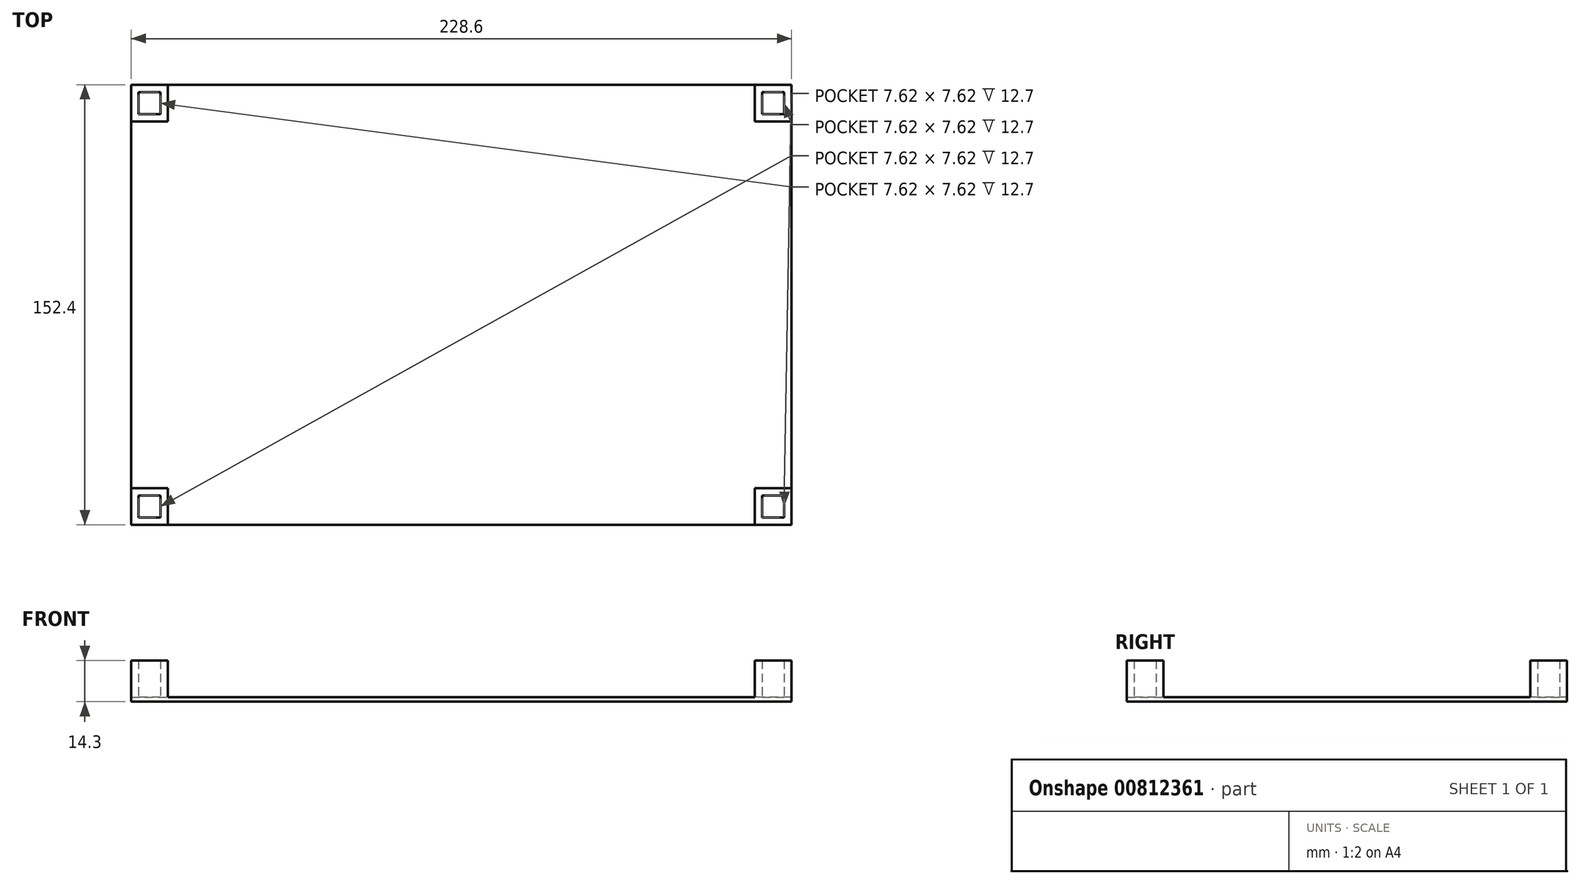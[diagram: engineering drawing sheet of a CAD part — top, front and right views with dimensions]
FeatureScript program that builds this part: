
annotation { "Feature Type Name" : "Feature", "Feature Type Description" : "" }
export const myFeature = defineFeature(function(context is Context, id is Id, definition is map)
    precondition{}
    {
        {
            var Q0;
            Q0=qCreatedBy(makeId("Top.planeOp"),FACE);
            var sketch = newSketch(context, id + "F0", { "sketchPlane" : qUnion([Q0])});
            skLineSegment(sketch, "E0.bottom", {"start": v(114.3, -76.2) * mm, "end": v(-114.3, -76.2) * mm});
            skLineSegment(sketch, "E0.top", {"start": v(114.3, 76.2) * mm, "end": v(-114.3, 76.2) * mm});
            skLineSegment(sketch, "E0.left", {"start": v(114.3, -76.2) * mm, "end": v(114.3, 76.2) * mm});
            skLineSegment(sketch, "E0.right", {"start": v(-114.3, -76.2) * mm, "end": v(-114.3, 76.2) * mm});
            skPoint(sketch, "E0.middle", {"position": v(0, 0) * mm});
            skSolve(sketch);
        }
        {
            var Q0;
            Q0=makeQuery(id+"F0.imprint","IMPRINT",FACE,{"disambiguationData":[TD([[makeQuery(id+"F0.imprint","IMPRINT",EDGE,{"derivedFrom":sQuery(id+"F0.wireOp",EDGE,"E0.bottom")}),-1.0]])]});
            extrude(context, id + "F1", {"entities" : qUnion([Q0]), "depth" : 1.6 * mm, "offsetDistance" : 25.4 * mm});
        }
        {
            var Q0;
            Q0=makeQuery(id+"F1.opExtrude","CAP_FACE",FACE,{"disambiguationData":[OSD([sQuery(id+"F0.wireOp",EDGE,"E0.bottom"),sQuery(id+"F0.wireOp",EDGE,"E0.top"),sQuery(id+"F0.wireOp",EDGE,"E0.left"),sQuery(id+"F0.wireOp",EDGE,"E0.right")])],"isStart":false});
            var sketch = newSketch(context, id + "F2", { "sketchPlane" : qUnion([Q0])});
            skLineSegment(sketch, "E1.bottom", {"start": v(114.3, -76.2) * mm, "end": v(101.6, -76.2) * mm});
            skLineSegment(sketch, "E1.top", {"start": v(114.3, -63.5) * mm, "end": v(101.6, -63.5) * mm});
            skLineSegment(sketch, "E1.left", {"start": v(114.3, -76.2) * mm, "end": v(114.3, -63.5) * mm});
            skLineSegment(sketch, "E1.right", {"start": v(101.6, -76.2) * mm, "end": v(101.6, -63.5) * mm});
            skLineSegment(sketch, "E2.bottom", {"start": v(104.14, -66.04) * mm, "end": v(111.76, -66.04) * mm});
            skLineSegment(sketch, "E2.top", {"start": v(104.14, -73.66) * mm, "end": v(111.76, -73.66) * mm});
            skLineSegment(sketch, "E2.left", {"start": v(104.14, -66.04) * mm, "end": v(104.14, -73.66) * mm});
            skLineSegment(sketch, "E2.right", {"start": v(111.76, -66.04) * mm, "end": v(111.76, -73.66) * mm});
            skLineSegment(sketch, "E3.MirrorCS", {"start": v(101.6, 76.2) * mm, "end": v(101.6, 63.5) * mm});
            skLineSegment(sketch, "E4.MirrorCS", {"start": v(114.3, 63.5) * mm, "end": v(101.6, 63.5) * mm});
            skLineSegment(sketch, "E5.MirrorCS", {"start": v(114.3, 76.2) * mm, "end": v(114.3, 63.5) * mm});
            skLineSegment(sketch, "E6.MirrorCS", {"start": v(114.3, 76.2) * mm, "end": v(101.6, 76.2) * mm});
            skLineSegment(sketch, "E7.MirrorCS", {"start": v(104.14, 73.66) * mm, "end": v(111.76, 73.66) * mm});
            skLineSegment(sketch, "E8.MirrorCS", {"start": v(111.76, 66.04) * mm, "end": v(111.76, 73.66) * mm});
            skLineSegment(sketch, "E9.MirrorCS", {"start": v(104.14, 66.04) * mm, "end": v(111.76, 66.04) * mm});
            skLineSegment(sketch, "E10.MirrorCS", {"start": v(104.14, 66.04) * mm, "end": v(104.14, 73.66) * mm});
            skLineSegment(sketch, "E11.MirrorCS", {"start": v(-101.6, -76.2) * mm, "end": v(-101.6, -63.5) * mm});
            skLineSegment(sketch, "E12.MirrorCS", {"start": v(-104.14, -66.04) * mm, "end": v(-104.14, -73.66) * mm});
            skLineSegment(sketch, "E13.MirrorCS", {"start": v(-111.76, -66.04) * mm, "end": v(-111.76, -73.66) * mm});
            skLineSegment(sketch, "E14.MirrorCS", {"start": v(-104.14, -73.66) * mm, "end": v(-111.76, -73.66) * mm});
            skLineSegment(sketch, "E15.MirrorCS", {"start": v(-104.14, -66.04) * mm, "end": v(-111.76, -66.04) * mm});
            skLineSegment(sketch, "E16.MirrorCS", {"start": v(-114.3, -63.5) * mm, "end": v(-101.6, -63.5) * mm});
            skLineSegment(sketch, "E17.MirrorCS", {"start": v(-114.3, -76.2) * mm, "end": v(-114.3, -63.5) * mm});
            skLineSegment(sketch, "E18.MirrorCS", {"start": v(-114.3, -76.2) * mm, "end": v(-101.6, -76.2) * mm});
            skLineSegment(sketch, "E19.MirrorCS", {"start": v(-101.6, 76.2) * mm, "end": v(-101.6, 63.5) * mm});
            skLineSegment(sketch, "E20.MirrorCS", {"start": v(-114.3, 76.2) * mm, "end": v(-101.6, 76.2) * mm});
            skLineSegment(sketch, "E21.MirrorCS", {"start": v(-114.3, 76.2) * mm, "end": v(-114.3, 63.5) * mm});
            skLineSegment(sketch, "E22.MirrorCS", {"start": v(-114.3, 63.5) * mm, "end": v(-101.6, 63.5) * mm});
            skLineSegment(sketch, "E23.MirrorCS", {"start": v(-104.14, 66.04) * mm, "end": v(-111.76, 66.04) * mm});
            skLineSegment(sketch, "E24.MirrorCS", {"start": v(-104.14, 66.04) * mm, "end": v(-104.14, 73.66) * mm});
            skLineSegment(sketch, "E25.MirrorCS", {"start": v(-111.76, 66.04) * mm, "end": v(-111.76, 73.66) * mm});
            skLineSegment(sketch, "E26.MirrorCS", {"start": v(-104.14, 73.66) * mm, "end": v(-111.76, 73.66) * mm});
            skSolve(sketch);
        }
        {
            var Q0;
            Q0=makeQuery(id+"F2.imprint","IMPRINT",FACE,{"disambiguationData":[TD([[makeQuery(id+"F2.imprint","IMPRINT",EDGE,{"derivedFrom":sQuery(id+"F2.wireOp",EDGE,"E19.MirrorCS")}),-1.0]])]});
            var Q1;
            Q1=makeQuery(id+"F2.imprint","IMPRINT",FACE,{"disambiguationData":[TD([[makeQuery(id+"F2.imprint","IMPRINT",EDGE,{"derivedFrom":sQuery(id+"F2.wireOp",EDGE,"E11.MirrorCS")}),1.0]])]});
            var Q2;
            Q2=makeQuery(id+"F2.imprint","IMPRINT",FACE,{"disambiguationData":[TD([[makeQuery(id+"F2.imprint","IMPRINT",EDGE,{"derivedFrom":sQuery(id+"F2.wireOp",EDGE,"E1.bottom")}),-1.0]])]});
            var Q3;
            Q3=makeQuery(id+"F2.imprint","IMPRINT",FACE,{"disambiguationData":[TD([[makeQuery(id+"F2.imprint","IMPRINT",EDGE,{"derivedFrom":sQuery(id+"F2.wireOp",EDGE,"E3.MirrorCS")}),1.0]])]});
            extrude(context, id + "F3", {"entities" : qUnion([Q0, Q1, Q2, Q3]), "operationType" : NewBodyOperationType.ADD, "depth" : 12.7 * mm, "offsetDistance" : 25.4 * mm});
        }
    });
